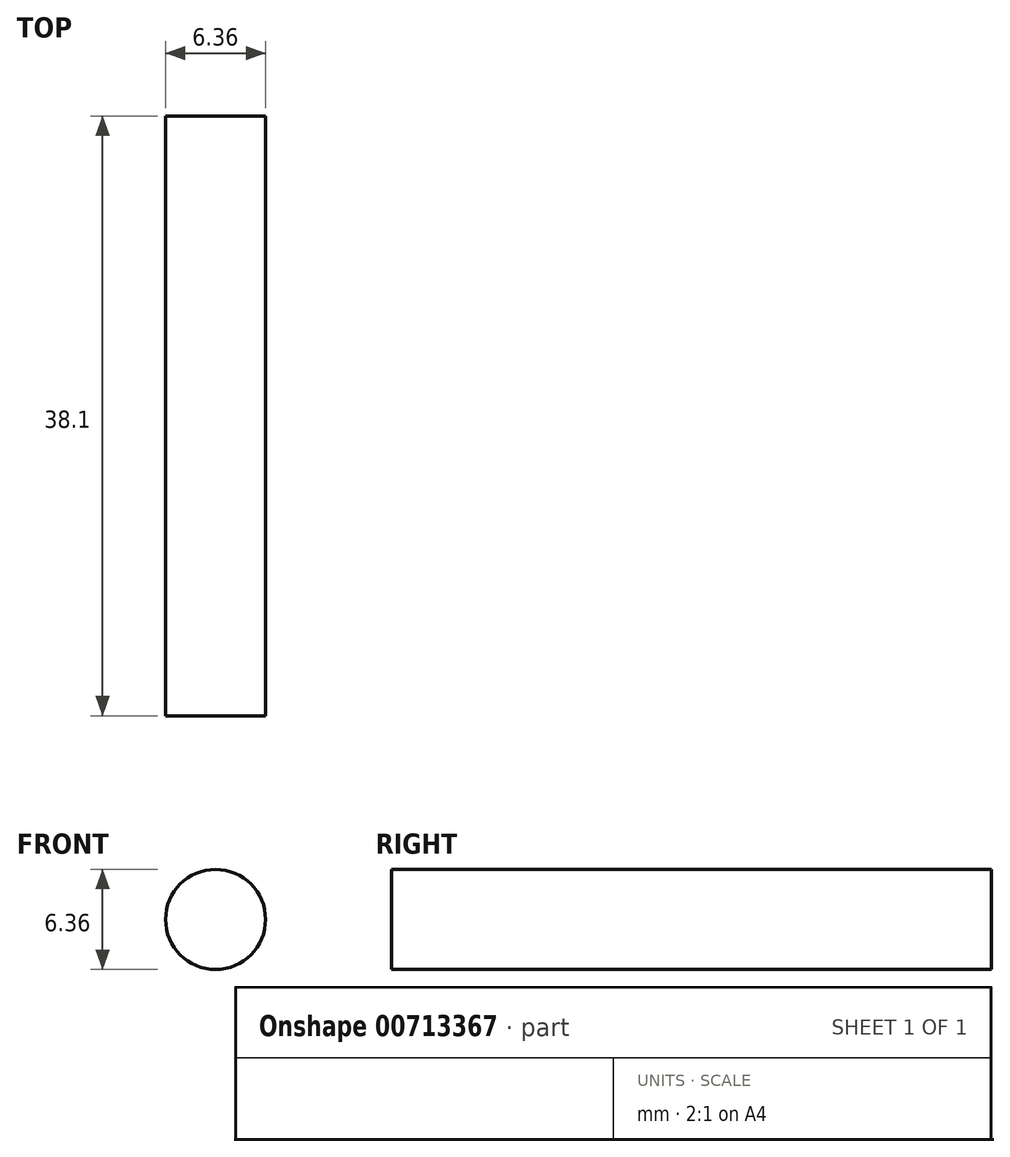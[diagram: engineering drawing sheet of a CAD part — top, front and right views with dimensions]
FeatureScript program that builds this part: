
annotation { "Feature Type Name" : "Feature", "Feature Type Description" : "" }
export const myFeature = defineFeature(function(context is Context, id is Id, definition is map)
    precondition{}
    {
        {
            var Q0;
            Q0=qCreatedBy(makeId("Front.planeOp"),FACE);
            var sketch = newSketch(context, id + "F0", { "sketchPlane" : qUnion([Q0])});
            skCircle(sketch, "E0", {"center": v(0, 0) * mm, "radius": 3.18 * mm});
            skSolve(sketch);
        }
        {
            var Q0;
            Q0 = qSketchRegion(id + "F0", true);
            extrude(context, id + "F1", {"entities" : qUnion([Q0]), "depth" : 38.1 * mm, "offsetDistance" : 25.4 * mm});
        }
    });
